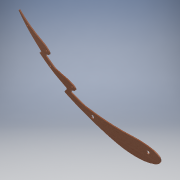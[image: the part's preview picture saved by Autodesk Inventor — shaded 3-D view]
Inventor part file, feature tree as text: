
AUTODESK INVENTOR PART (.ipt)
format: ipt  version: 2018 (Build 220112000, 112)  size: 201,216 bytes
history: native  units: mm
features: other x7, reference x6, projected_geometry x3, extrude x2, sketch x2, fillet x1
ambient origin geometry x8: Origin, YZ Plane, XZ Plane, XY Plane, X Axis, Y Axis, Z Axis, Center Point
bodies: Body1 (feature_tree)
feature tree (21):
  extrude  "押し出し1"  TaperAngle=45.0deg  [1 undecoded]
  fillet  "フィレット1"  [1 undecoded]
  extrude  "押し出し2"  Depth=60.0mm
  sketch  "スケッチ1"
  projected_geometry  "投影ループ1"
  projected_geometry  "投影ループ2"
  projected_geometry  "投影ループ3"
  sketch  "スケッチ2"
  reference  "参照1"
  reference  "参照2"
  reference  "参照3"
  reference  "参照4"
  reference  "参照5"
  reference  "参照6"
  other  "<userpath>\Documents\Inventor\Aero\KS-15\Rr.wing\Rr.wing_assy.iam"
  other  "Rr.wing_assy.iam"
  other  "mainflap:1"
  other  "flap_m:1"
  other  "subflap:3"
  other  "flap_s:1"
  other  "subflap:8"
note: 2 required parameter values undecoded (feature->parameter linkage not recoverable at this tier; creation-order binding heuristic only, values carry confidence <= 0.55)
